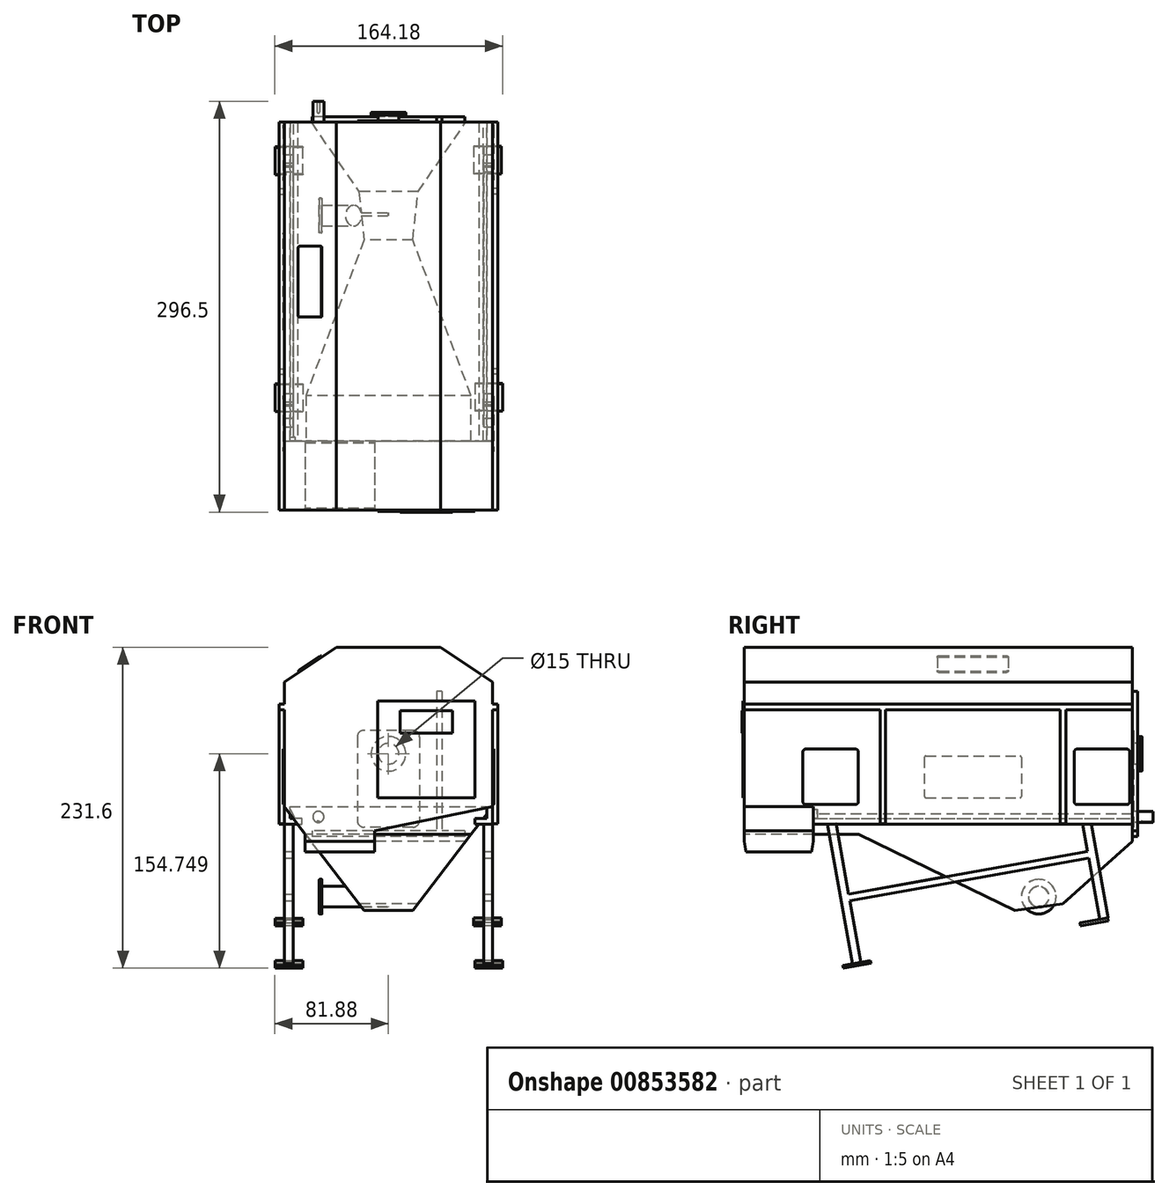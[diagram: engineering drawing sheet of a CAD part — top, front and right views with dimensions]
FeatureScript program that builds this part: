
annotation { "Feature Type Name" : "Feature", "Feature Type Description" : "" }
export const myFeature = defineFeature(function(context is Context, id is Id, definition is map)
    precondition{}
    {
        {
            var Q0;
            Q0=qCreatedBy(makeId("Front.planeOp"),FACE);
            var sketch = newSketch(context, id + "F0", { "sketchPlane" : qUnion([Q0])});
            skLineSegment(sketch, "E0", {"start": v(0, 115) * mm, "end": v(0, -89.09) * mm, "construction": true});
            skLineSegment(sketch, "E1", {"start": v(-37.5, 115) * mm, "end": v(37.5, 115) * mm});
            skLineSegment(sketch, "E2", {"start": v(37.5, 115) * mm, "end": v(75, 90) * mm});
            skLineSegment(sketch, "E3", {"start": v(75, 90) * mm, "end": v(75, 0) * mm});
            skLineSegment(sketch, "E4", {"start": v(75, 0) * mm, "end": v(-75, 0) * mm});
            skLineSegment(sketch, "E5", {"start": v(-75, 0) * mm, "end": v(-75, 90) * mm});
            skLineSegment(sketch, "E6", {"start": v(-75, 90) * mm, "end": v(-37.5, 115) * mm});
            skSolve(sketch);
        }
        {
            var Q0;
            Q0=makeQuery(id+"F0.imprint","IMPRINT",FACE,{"disambiguationData":[TD([[makeQuery(id+"F0.imprint","IMPRINT",EDGE,{"derivedFrom":sQuery(id+"F0.wireOp",EDGE,"E1")}),-1.0]])]});
            extrude(context, id + "F1", {"entities" : qUnion([Q0]), "oppositeDirection" : true, "depth" : 280 * mm, "offsetDistance" : 25 * mm});
        }
        {
            var Q0;
            Q0=qCreatedBy(makeId("Front.planeOp"),FACE);
            var sketch = newSketch(context, id + "F2", { "sketchPlane" : qUnion([Q0])});
            skLineSegment(sketch, "E7", {"start": v(-75, 0) * mm, "end": v(-60, -20) * mm});
            skLineSegment(sketch, "E8", {"start": v(-60, -20) * mm, "end": v(-60, -32.5) * mm});
            skLineSegment(sketch, "E9", {"start": v(-60, -32.5) * mm, "end": v(-10, -32.5) * mm});
            skLineSegment(sketch, "E10", {"start": v(-75, 0) * mm, "end": v(75, 0) * mm});
            skLineSegment(sketch, "E11", {"start": v(-10, -32.5) * mm, "end": v(-10, -17.5) * mm});
            skLineSegment(sketch, "E12", {"start": v(-10, -17.5) * mm, "end": v(75, 0) * mm});
            skSolve(sketch);
        }
        {
            var Q0;
            Q0=qCreatedBy(makeId("Right.planeOp"),FACE);
            var sketch = newSketch(context, id + "F3", { "sketchPlane" : qUnion([Q0])});
            skLineSegment(sketch, "E13", {"start": v(280, 0) * mm, "end": v(52.63, 0) * mm});
            skLineSegment(sketch, "E14", {"start": v(229.78, -70) * mm, "end": v(195.13, -75) * mm});
            skLineSegment(sketch, "E15", {"start": v(195.13, -75) * mm, "end": v(82.63, -20) * mm});
            skLineSegment(sketch, "E16", {"start": v(82.63, -20) * mm, "end": v(52.63, -20) * mm});
            skLineSegment(sketch, "E17", {"start": v(52.63, 0) * mm, "end": v(52.63, -20) * mm});
            skLineSegment(sketch, "E18", {"start": v(280, 0) * mm, "end": v(280, -25) * mm});
            skLineSegment(sketch, "E19", {"start": v(280, -25) * mm, "end": v(229.78, -70) * mm});
            skSolve(sketch);
        }
        {
            var Q0;
            Q0=makeQuery(id+"F3.imprint","IMPRINT",FACE,{"disambiguationData":[TD([[makeQuery(id+"F3.imprint","IMPRINT",EDGE,{"derivedFrom":sQuery(id+"F3.wireOp",EDGE,"E13")}),1.0]])]});
            extrude(context, id + "F4", {"entities" : qUnion([Q0]), "operationType" : NewBodyOperationType.ADD, "endBound" : BoundingType.SYMMETRIC, "depth" : 150 * mm, "offsetDistance" : 25 * mm});
        }
        {
            var Q0;
            Q0=makeQuery(id+"F4.boolean.opBoolean","MERGE",FACE,{"derivedFrom":[makeQuery(id+"F1.opExtrude","CAP_FACE",FACE,{"disambiguationData":[OSD([sQuery(id+"F0.wireOp",EDGE,"E1"),sQuery(id+"F0.wireOp",EDGE,"E2"),sQuery(id+"F0.wireOp",EDGE,"E3"),sQuery(id+"F0.wireOp",EDGE,"E4"),sQuery(id+"F0.wireOp",EDGE,"E5"),sQuery(id+"F0.wireOp",EDGE,"E6")])],"isStart":false}),makeQuery(id+"F4.opExtrude","SWEPT_FACE",FACE,{"disambiguationData":[OSD([sQuery(id+"F3.wireOp",EDGE,"E18")])]})]});
            var sketch = newSketch(context, id + "F5", { "sketchPlane" : qUnion([Q0])});
            skLineSegment(sketch, "E20", {"start": v(75, -75) * mm, "end": v(75, 0) * mm});
            skLineSegment(sketch, "E21", {"start": v(75, 0) * mm, "end": v(17.5, -75) * mm});
            skLineSegment(sketch, "E22", {"start": v(17.5, -75) * mm, "end": v(75, -75) * mm});
            skLineSegment(sketch, "E23", {"start": v(-75, 0) * mm, "end": v(-75, -75) * mm});
            skLineSegment(sketch, "E24", {"start": v(-75, -75) * mm, "end": v(-17.5, -75) * mm});
            skLineSegment(sketch, "E25", {"start": v(-17.5, -75) * mm, "end": v(-75, 0) * mm});
            skSolve(sketch);
        }
        {
            var Q0;
            Q0 = qSketchRegion(id + "F5", true);
            extrude(context, id + "F6", {"entities" : qUnion([Q0]), "operationType" : NewBodyOperationType.REMOVE, "oppositeDirection" : true, "depth" : 280 * mm, "offsetDistance" : 25 * mm});
        }
        {
            var Q0;
            Q0=makeQuery(id+"F2.imprint","IMPRINT",FACE,{"disambiguationData":[TD([[makeQuery(id+"F2.imprint","IMPRINT",EDGE,{"derivedFrom":sQuery(id+"F2.wireOp",EDGE,"E7")}),1.0]])]});
            extrude(context, id + "F7", {"entities" : qUnion([Q0]), "operationType" : NewBodyOperationType.ADD, "oppositeDirection" : true, "depth" : 50 * mm, "offsetDistance" : 25 * mm});
        }
        {
            var Q0;
            Q0=makeQuery(id+"F4.boolean.opBoolean","MERGE",FACE,{"derivedFrom":[makeQuery(id+"F1.opExtrude","CAP_FACE",FACE,{"disambiguationData":[OSD([sQuery(id+"F0.wireOp",EDGE,"E1"),sQuery(id+"F0.wireOp",EDGE,"E2"),sQuery(id+"F0.wireOp",EDGE,"E3"),sQuery(id+"F0.wireOp",EDGE,"E4"),sQuery(id+"F0.wireOp",EDGE,"E5"),sQuery(id+"F0.wireOp",EDGE,"E6")])],"isStart":false}),makeQuery(id+"F4.opExtrude","SWEPT_FACE",FACE,{"disambiguationData":[OSD([sQuery(id+"F3.wireOp",EDGE,"E18")])]})]});
            var sketch = newSketch(context, id + "F8", { "sketchPlane" : qUnion([Q0])});
            skLineSegment(sketch, "E26", {"start": v(75, 0) * mm, "end": v(75, -12.5) * mm});
            skLineSegment(sketch, "E27", {"start": v(75, -12.5) * mm, "end": v(62.5, -12.5) * mm});
            skLineSegment(sketch, "E28", {"start": v(62.5, -12.5) * mm, "end": v(62.5, -8.5) * mm});
            skLineSegment(sketch, "E29", {"start": v(62.5, -8.5) * mm, "end": v(71, -8.5) * mm});
            skLineSegment(sketch, "E30", {"start": v(71, -8.5) * mm, "end": v(71, 0) * mm});
            skLineSegment(sketch, "E31", {"start": v(71, 0) * mm, "end": v(75, 0) * mm});
            skSolve(sketch);
        }
        {
            var Q0;
            Q0 = qSketchRegion(id + "F8", true);
            extrude(context, id + "F9", {"entities" : qUnion([Q0]), "operationType" : NewBodyOperationType.ADD, "oppositeDirection" : true, "depth" : 230 * mm, "offsetDistance" : 25 * mm});
        }
        {
            var Q0;
            Q0=makeQuery(id+"F9.boolean.opBoolean","MERGE",FACE,{"derivedFrom":[makeQuery(id+"F4.boolean.opBoolean","MERGE",FACE,{"derivedFrom":[makeQuery(id+"F1.opExtrude","CAP_FACE",FACE,{"disambiguationData":[OSD([sQuery(id+"F0.wireOp",EDGE,"E1"),sQuery(id+"F0.wireOp",EDGE,"E2"),sQuery(id+"F0.wireOp",EDGE,"E3"),sQuery(id+"F0.wireOp",EDGE,"E4"),sQuery(id+"F0.wireOp",EDGE,"E5"),sQuery(id+"F0.wireOp",EDGE,"E6")])],"isStart":false}),makeQuery(id+"F4.opExtrude","SWEPT_FACE",FACE,{"disambiguationData":[OSD([sQuery(id+"F3.wireOp",EDGE,"E18")])]})]}),makeQuery(id+"F9.opExtrude","CAP_FACE",FACE,{"disambiguationData":[OSD([sQuery(id+"F8.wireOp",EDGE,"E26"),sQuery(id+"F8.wireOp",EDGE,"E27"),sQuery(id+"F8.wireOp",EDGE,"E28"),sQuery(id+"F8.wireOp",EDGE,"E29"),sQuery(id+"F8.wireOp",EDGE,"E30"),sQuery(id+"F8.wireOp",EDGE,"E31")])],"isStart":true})]});
            var sketch = newSketch(context, id + "F10", { "sketchPlane" : qUnion([Q0])});
            skLineSegment(sketch, "E32", {"start": v(-75, 0) * mm, "end": v(-75, -12.5) * mm});
            skLineSegment(sketch, "E33", {"start": v(-75, -12.5) * mm, "end": v(-62.5, -12.5) * mm});
            skLineSegment(sketch, "E34", {"start": v(-62.5, -12.5) * mm, "end": v(-62.5, -8.5) * mm});
            skLineSegment(sketch, "E35", {"start": v(-62.5, -8.5) * mm, "end": v(-71, -8.5) * mm});
            skLineSegment(sketch, "E36", {"start": v(-71, -8.5) * mm, "end": v(-71, 0) * mm});
            skLineSegment(sketch, "E37", {"start": v(-71, 0) * mm, "end": v(-75, 0) * mm});
            skSolve(sketch);
        }
        {
            var Q0;
            Q0 = qSketchRegion(id + "F10", true);
            extrude(context, id + "F11", {"entities" : qUnion([Q0]), "operationType" : NewBodyOperationType.ADD, "oppositeDirection" : true, "depth" : 230 * mm, "offsetDistance" : 25 * mm});
        }
        {
            var Q0;
            Q0=makeQuery(id+"F4.boolean.opBoolean","MERGE",FACE,{"derivedFrom":[makeQuery(id+"F1.opExtrude","SWEPT_FACE",FACE,{"disambiguationData":[OSD([sQuery(id+"F0.wireOp",EDGE,"E3")])]}),makeQuery(id+"F4.opExtrude","CAP_FACE",FACE,{"disambiguationData":[OSD([sQuery(id+"F3.wireOp",EDGE,"E13"),sQuery(id+"F3.wireOp",EDGE,"E14"),sQuery(id+"F3.wireOp",EDGE,"E15"),sQuery(id+"F3.wireOp",EDGE,"E16"),sQuery(id+"F3.wireOp",EDGE,"E17"),sQuery(id+"F3.wireOp",EDGE,"E18"),sQuery(id+"F3.wireOp",EDGE,"E19")])],"isStart":false})]});
            var sketch = newSketch(context, id + "F12", { "sketchPlane" : qUnion([Q0])});
            skLineSegment(sketch, "E38", {"start": v(60, -12.5) * mm, "end": v(78.1, -113.4) * mm});
            skLineSegment(sketch, "E39", {"start": v(78.1, -113.4) * mm, "end": v(84.24, -112.29) * mm});
            skLineSegment(sketch, "E40", {"start": v(84.24, -112.29) * mm, "end": v(76.3, -68) * mm});
            skLineSegment(sketch, "E41", {"start": v(76.3, -68) * mm, "end": v(248.55, -37.1) * mm});
            skLineSegment(sketch, "E42", {"start": v(248.55, -37.1) * mm, "end": v(256.5, -81.4) * mm});
            skLineSegment(sketch, "E43", {"start": v(256.5, -81.4) * mm, "end": v(262.65, -80.3) * mm});
            skLineSegment(sketch, "E44", {"start": v(262.65, -80.3) * mm, "end": v(250.56, -12.87) * mm});
            skLineSegment(sketch, "E45", {"start": v(247.67, -32.19) * mm, "end": v(75.42, -63.07) * mm});
            skLineSegment(sketch, "E46", {"start": v(75.42, -63.07) * mm, "end": v(66.33, -12.38) * mm});
            skLineSegment(sketch, "E47", {"start": v(66.33, -12.38) * mm, "end": v(60, -12.5) * mm});
            skLineSegment(sketch, "E48", {"start": v(247.67, -32.19) * mm, "end": v(244.14, -12.5) * mm});
            skLineSegment(sketch, "E49", {"start": v(244.14, -12.5) * mm, "end": v(250.56, -12.87) * mm});
            skLineSegment(sketch, "E50", {"start": v(50, -12.5) * mm, "end": v(60, -12.5) * mm, "construction": true});
            skSolve(sketch);
        }
        {
            var Q0;
            Q0 = qSketchRegion(id + "F12", true);
            extrude(context, id + "F13", {"entities" : qUnion([Q0]), "oppositeDirection" : true, "depth" : 6.25 * mm, "offsetDistance" : 25 * mm});
        }
        {
            var Q0;
            Q0=makeQuery(id+"F13.opExtrude","SWEPT_BODY",BODY,{"disambiguationData":[OSD([sQuery(id+"F12.wireOp",EDGE,"E38"),sQuery(id+"F12.wireOp",EDGE,"E39"),sQuery(id+"F12.wireOp",EDGE,"E40"),sQuery(id+"F12.wireOp",EDGE,"E41"),sQuery(id+"F12.wireOp",EDGE,"E42"),sQuery(id+"F12.wireOp",EDGE,"E43"),sQuery(id+"F12.wireOp",EDGE,"E44"),sQuery(id+"F12.wireOp",EDGE,"E45"),sQuery(id+"F12.wireOp",EDGE,"E46"),sQuery(id+"F12.wireOp",EDGE,"E47"),sQuery(id+"F12.wireOp",EDGE,"E48"),sQuery(id+"F12.wireOp",EDGE,"E49")])]});
            transform(context, id + "F14", {"entities" : qUnion([Q0]), "transformType" : TransformType.TRANSLATION_3D, "dx" : 150 * mm, "dy" : 0 * mm, "dz" : 0 * mm, "makeCopy" : true});
        }
        {
            var Q0;
            Q0=makeQuery(id+"F14.opPattern","COPY",BODY,{"derivedFrom":makeQuery(id+"F13.opExtrude","SWEPT_BODY",BODY,{"disambiguationData":[OSD([sQuery(id+"F12.wireOp",EDGE,"E38"),sQuery(id+"F12.wireOp",EDGE,"E39"),sQuery(id+"F12.wireOp",EDGE,"E40"),sQuery(id+"F12.wireOp",EDGE,"E41"),sQuery(id+"F12.wireOp",EDGE,"E42"),sQuery(id+"F12.wireOp",EDGE,"E43"),sQuery(id+"F12.wireOp",EDGE,"E44"),sQuery(id+"F12.wireOp",EDGE,"E45"),sQuery(id+"F12.wireOp",EDGE,"E46"),sQuery(id+"F12.wireOp",EDGE,"E47"),sQuery(id+"F12.wireOp",EDGE,"E48"),sQuery(id+"F12.wireOp",EDGE,"E49")])]}),"instanceName":"1"});
            deleteBodies(context, id + "F15", {"entities" : qUnion([Q0])});
        }
        {
            var Q0;
            Q0=makeQuery(id+"F13.opExtrude","SWEPT_BODY",BODY,{"disambiguationData":[OSD([sQuery(id+"F12.wireOp",EDGE,"E38"),sQuery(id+"F12.wireOp",EDGE,"E39"),sQuery(id+"F12.wireOp",EDGE,"E40"),sQuery(id+"F12.wireOp",EDGE,"E41"),sQuery(id+"F12.wireOp",EDGE,"E42"),sQuery(id+"F12.wireOp",EDGE,"E43"),sQuery(id+"F12.wireOp",EDGE,"E44"),sQuery(id+"F12.wireOp",EDGE,"E45"),sQuery(id+"F12.wireOp",EDGE,"E46"),sQuery(id+"F12.wireOp",EDGE,"E47"),sQuery(id+"F12.wireOp",EDGE,"E48"),sQuery(id+"F12.wireOp",EDGE,"E49")])]});
            transform(context, id + "F16", {"entities" : qUnion([Q0]), "transformType" : TransformType.TRANSLATION_3D, "dx" : -143.75 * mm, "dy" : 0 * mm, "dz" : 0 * mm, "makeCopy" : true});
        }
        {
            var Q0;
            Q0=makeQuery(id+"F7.opExtrude","SWEPT_FACE",FACE,{"disambiguationData":[OSD([sQuery(id+"F2.wireOp",EDGE,"E11")])]});
            var sketch = newSketch(context, id + "F17", { "sketchPlane" : qUnion([Q0])});
            skLineSegment(sketch, "E51.bottom", {"start": v(-2.7, -21.26) * mm, "end": v(-0.73, -20.9) * mm});
            skLineSegment(sketch, "E51.top", {"start": v(-0.05, -36.03) * mm, "end": v(1.91, -35.67) * mm});
            skLineSegment(sketch, "E51.left", {"start": v(-2.7, -21.26) * mm, "end": v(-0.05, -36.03) * mm});
            skLineSegment(sketch, "E51.right", {"start": v(-0.73, -20.9) * mm, "end": v(1.91, -35.67) * mm});
            skSolve(sketch);
        }
        {
            var Q0;
            Q0 = qSketchRegion(id + "F17", true);
            extrude(context, id + "F18", {"entities" : qUnion([Q0]), "operationType" : NewBodyOperationType.REMOVE, "oppositeDirection" : true, "depth" : 50 * mm, "offsetDistance" : 25 * mm});
        }
        {
            var Q0;
            Q0=makeQuery(id+"F7.opExtrude","SWEPT_FACE",FACE,{"disambiguationData":[OSD([sQuery(id+"F2.wireOp",EDGE,"E8")])]});
            var sketch = newSketch(context, id + "F19", { "sketchPlane" : qUnion([Q0])});
            skLineSegment(sketch, "E52.bottom", {"start": v(-52.12, -24.53) * mm, "end": v(-50.15, -24.17) * mm});
            skLineSegment(sketch, "E52.top", {"start": v(-49.47, -39.3) * mm, "end": v(-47.5, -38.94) * mm});
            skLineSegment(sketch, "E52.left", {"start": v(-52.12, -24.53) * mm, "end": v(-49.47, -39.3) * mm});
            skLineSegment(sketch, "E52.right", {"start": v(-50.15, -24.17) * mm, "end": v(-47.5, -38.94) * mm});
            skLineSegment(sketch, "E53", {"start": v(0, -25) * mm, "end": v(-50, -25) * mm, "construction": true});
            skSolve(sketch);
        }
        {
            var Q0;
            Q0 = qSketchRegion(id + "F19", true);
            extrude(context, id + "F20", {"entities" : qUnion([Q0]), "operationType" : NewBodyOperationType.REMOVE, "oppositeDirection" : true, "depth" : 50 * mm, "offsetDistance" : 25 * mm});
        }
        {
            var Q0;
            Q0=qCreatedBy(makeId("Right.planeOp"),FACE);
            var sketch = newSketch(context, id + "F21", { "sketchPlane" : qUnion([Q0])});
            skCircle(sketch, "E54", {"center": v(212.51, -65) * mm, "radius": 7.5 * mm});
            skPoint(sketch, "E54.first.point", {"position": v(212.45, -72.5) * mm});
            skPoint(sketch, "E54.second.point", {"position": v(213.2, -57.53) * mm});
            skPoint(sketch, "E54.third.point", {"position": v(205.16, -63.52) * mm});
            skSolve(sketch);
        }
        {
            var Q0;
            Q0 = qSketchRegion(id + "F21", true);
            extrude(context, id + "F22", {"entities" : qUnion([Q0]), "operationType" : NewBodyOperationType.ADD, "oppositeDirection" : true, "depth" : 50 * mm, "offsetDistance" : 25 * mm});
        }
        {
            var Q0;
            Q0=makeQuery(id+"F22.opExtrude","CAP_FACE",FACE,{"disambiguationData":[OSD([sQuery(id+"F21.wireOp",EDGE,"E54")])],"isStart":false});
            var sketch = newSketch(context, id + "F23", { "sketchPlane" : qUnion([Q0])});
            skCircle(sketch, "E55", {"center": v(-212.51, -65) * mm, "radius": 12.5 * mm});
            skSolve(sketch);
        }
        {
            var Q0;
            Q0 = qSketchRegion(id + "F23", true);
            extrude(context, id + "F24", {"entities" : qUnion([Q0]), "operationType" : NewBodyOperationType.ADD, "oppositeDirection" : true, "depth" : 2 * mm, "offsetDistance" : 25 * mm});
        }
        {
            var Q0;
            Q0=makeQuery(id+"F24.opExtrude","SWEPT_FACE",FACE,{"disambiguationData":[OSD([sQuery(id+"F23.wireOp",EDGE,"E55")])]});
            fillet(context, id + "F25", {"entities" : qUnion([Q0]), "radius" : 0.25 * mm, "tangentPropagation" : true, "allowEdgeOverflow" : false});
        }
        {
            var Q0;
            Q0=makeQuery(id+"F11.boolean.opBoolean","MERGE",FACE,{"derivedFrom":[makeQuery(id+"F9.boolean.opBoolean","MERGE",FACE,{"derivedFrom":[makeQuery(id+"F4.boolean.opBoolean","MERGE",FACE,{"derivedFrom":[makeQuery(id+"F1.opExtrude","CAP_FACE",FACE,{"disambiguationData":[OSD([sQuery(id+"F0.wireOp",EDGE,"E1"),sQuery(id+"F0.wireOp",EDGE,"E2"),sQuery(id+"F0.wireOp",EDGE,"E3"),sQuery(id+"F0.wireOp",EDGE,"E4"),sQuery(id+"F0.wireOp",EDGE,"E5"),sQuery(id+"F0.wireOp",EDGE,"E6")])],"isStart":false}),makeQuery(id+"F4.opExtrude","SWEPT_FACE",FACE,{"disambiguationData":[OSD([sQuery(id+"F3.wireOp",EDGE,"E18")])]})]}),makeQuery(id+"F9.opExtrude","CAP_FACE",FACE,{"disambiguationData":[OSD([sQuery(id+"F8.wireOp",EDGE,"E26"),sQuery(id+"F8.wireOp",EDGE,"E27"),sQuery(id+"F8.wireOp",EDGE,"E28"),sQuery(id+"F8.wireOp",EDGE,"E29"),sQuery(id+"F8.wireOp",EDGE,"E30"),sQuery(id+"F8.wireOp",EDGE,"E31")])],"isStart":true})]}),makeQuery(id+"F11.opExtrude","CAP_FACE",FACE,{"disambiguationData":[OSD([sQuery(id+"F10.wireOp",EDGE,"E32"),sQuery(id+"F10.wireOp",EDGE,"E33"),sQuery(id+"F10.wireOp",EDGE,"E34"),sQuery(id+"F10.wireOp",EDGE,"E35"),sQuery(id+"F10.wireOp",EDGE,"E36"),sQuery(id+"F10.wireOp",EDGE,"E37")])],"isStart":true})]});
            var sketch = newSketch(context, id + "F26", { "sketchPlane" : qUnion([Q0])});
            skLineSegment(sketch, "E56.bottom", {"start": v(-17.5, 55.1) * mm, "end": v(17.5, 55.1) * mm});
            skLineSegment(sketch, "E56.top", {"start": v(-17.5, -14.9) * mm, "end": v(17.5, -14.9) * mm});
            skLineSegment(sketch, "E56.left", {"start": v(-22.5, 50.1) * mm, "end": v(-22.5, -9.9) * mm});
            skLineSegment(sketch, "E56.right", {"start": v(22.5, 50.1) * mm, "end": v(22.5, -9.9) * mm});
            skPoint(sketch, "E57.visualSharp", {"position": v(22.5, 55.1) * mm});
            skArc(sketch, "E57.filletArc", {"start": v(22.5, 50.1) * mm, "mid": v(21.04, 53.64) * mm, "end": v(17.5, 55.1) * mm});
            skPoint(sketch, "E58.visualSharp", {"position": v(-22.5, 55.1) * mm});
            skArc(sketch, "E58.filletArc", {"start": v(-17.5, 55.1) * mm, "mid": v(-21.04, 53.64) * mm, "end": v(-22.5, 50.1) * mm});
            skPoint(sketch, "E59.visualSharp", {"position": v(-22.5, -14.9) * mm});
            skArc(sketch, "E59.filletArc", {"start": v(-22.5, -9.9) * mm, "mid": v(-21.04, -13.43) * mm, "end": v(-17.5, -14.9) * mm});
            skPoint(sketch, "E60.visualSharp", {"position": v(22.5, -14.9) * mm});
            skArc(sketch, "E60.filletArc", {"start": v(17.5, -14.9) * mm, "mid": v(21.04, -13.43) * mm, "end": v(22.5, -9.9) * mm});
            skLineSegment(sketch, "E61", {"start": v(0, -25) * mm, "end": v(0, 111.63) * mm, "construction": true});
            skCircle(sketch, "E62", {"center": v(0, 38.15) * mm, "radius": 7.5 * mm});
            skSolve(sketch);
        }
        {
            var Q0;
            Q0=makeQuery(id+"F26.imprint","IMPRINT",FACE,{"disambiguationData":[TD([[makeQuery(id+"F26.imprint","IMPRINT",EDGE,{"derivedFrom":sQuery(id+"F26.wireOp",EDGE,"E62")}),1.0]])]});
            var Q1;
            Q1=sQuery(id+"F26.wireOp",EDGE,"E62");
            extrude(context, id + "F27", {"entities" : qUnion([Q0]), "surfaceEntities" : qUnion([Q1]), "depth" : 5 * mm, "offsetDistance" : 25 * mm});
        }
        {
            var Q0;
            Q0=makeQuery(id+"F26.imprint","IMPRINT",FACE,{"disambiguationData":[TD([[makeQuery(id+"F26.imprint","IMPRINT",EDGE,{"derivedFrom":sQuery(id+"F26.wireOp",EDGE,"E56.bottom")}),-1.0]])]});
            extrude(context, id + "F28", {"entities" : qUnion([Q0]), "depth" : 1 * mm, "offsetDistance" : 25 * mm});
        }
        {
            var Q0;
            Q0=makeQuery(id+"F27.opExtrude","CAP_FACE",FACE,{"disambiguationData":[OSD([sQuery(id+"F26.wireOp",EDGE,"E62")])],"isStart":false});
            var sketch = newSketch(context, id + "F29", { "sketchPlane" : qUnion([Q0])});
            skCircle(sketch, "E63", {"center": v(0, 38.15) * mm, "radius": 12.5 * mm});
            skSolve(sketch);
        }
        {
            var Q0;
            Q0 = qSketchRegion(id + "F29", true);
            extrude(context, id + "F30", {"entities" : qUnion([Q0]), "operationType" : NewBodyOperationType.ADD, "depth" : 2 * mm, "offsetDistance" : 25 * mm});
        }
        {
            var Q0;
            Q0=makeQuery(id+"F30.opExtrude","SWEPT_FACE",FACE,{"disambiguationData":[OSD([sQuery(id+"F29.wireOp",EDGE,"E63")])]});
            fillet(context, id + "F31", {"entities" : qUnion([Q0]), "radius" : 0.25 * mm, "tangentPropagation" : true, "allowEdgeOverflow" : false});
        }
        {
            var Q0;
            Q0=makeQuery(id+"F11.boolean.opBoolean","MERGE",FACE,{"derivedFrom":[makeQuery(id+"F9.boolean.opBoolean","MERGE",FACE,{"derivedFrom":[makeQuery(id+"F4.boolean.opBoolean","MERGE",FACE,{"derivedFrom":[makeQuery(id+"F1.opExtrude","CAP_FACE",FACE,{"disambiguationData":[OSD([sQuery(id+"F0.wireOp",EDGE,"E1"),sQuery(id+"F0.wireOp",EDGE,"E2"),sQuery(id+"F0.wireOp",EDGE,"E3"),sQuery(id+"F0.wireOp",EDGE,"E4"),sQuery(id+"F0.wireOp",EDGE,"E5"),sQuery(id+"F0.wireOp",EDGE,"E6")])],"isStart":false}),makeQuery(id+"F4.opExtrude","SWEPT_FACE",FACE,{"disambiguationData":[OSD([sQuery(id+"F3.wireOp",EDGE,"E18")])]})]}),makeQuery(id+"F9.opExtrude","CAP_FACE",FACE,{"disambiguationData":[OSD([sQuery(id+"F8.wireOp",EDGE,"E26"),sQuery(id+"F8.wireOp",EDGE,"E27"),sQuery(id+"F8.wireOp",EDGE,"E28"),sQuery(id+"F8.wireOp",EDGE,"E29"),sQuery(id+"F8.wireOp",EDGE,"E30"),sQuery(id+"F8.wireOp",EDGE,"E31")])],"isStart":true})]}),makeQuery(id+"F11.opExtrude","CAP_FACE",FACE,{"disambiguationData":[OSD([sQuery(id+"F10.wireOp",EDGE,"E32"),sQuery(id+"F10.wireOp",EDGE,"E33"),sQuery(id+"F10.wireOp",EDGE,"E34"),sQuery(id+"F10.wireOp",EDGE,"E35"),sQuery(id+"F10.wireOp",EDGE,"E36"),sQuery(id+"F10.wireOp",EDGE,"E37")])],"isStart":true})]});
            var sketch = newSketch(context, id + "F32", { "sketchPlane" : qUnion([Q0])});
            skLineSegment(sketch, "E64", {"start": v(-55, -25) * mm, "end": v(-55, -14.86) * mm, "construction": true});
            skLineSegment(sketch, "E65", {"start": v(-55, -14.86) * mm, "end": v(-55, -19.93) * mm, "construction": true});
            skLineSegment(sketch, "E66.bottom", {"start": v(-55, -17.4) * mm, "end": v(55, -17.4) * mm});
            skLineSegment(sketch, "E66.top", {"start": v(-55, -21.4) * mm, "end": v(55, -21.4) * mm});
            skLineSegment(sketch, "E66.left", {"start": v(-55, -17.4) * mm, "end": v(-55, -21.4) * mm});
            skLineSegment(sketch, "E66.right", {"start": v(55, -17.4) * mm, "end": v(55, -21.4) * mm});
            skLineSegment(sketch, "E67", {"start": v(0, -25) * mm, "end": v(0, -21.4) * mm, "construction": true});
            skLineSegment(sketch, "E68", {"start": v(-36.67, -17.4) * mm, "end": v(-36.67, 83.32) * mm, "construction": true});
            skLineSegment(sketch, "E69.bottom", {"start": v(-38.67, 83.32) * mm, "end": v(-34.67, 83.32) * mm});
            skLineSegment(sketch, "E69.top", {"start": v(-38.67, -17.4) * mm, "end": v(-34.67, -17.4) * mm});
            skLineSegment(sketch, "E69.left", {"start": v(-38.67, 83.32) * mm, "end": v(-38.67, -17.4) * mm});
            skLineSegment(sketch, "E69.right", {"start": v(-34.67, 83.32) * mm, "end": v(-34.67, -17.4) * mm});
            skPoint(sketch, "E69.middle", {"position": v(-36.67, 32.96) * mm});
            skSolve(sketch);
        }
        {
            var Q0;
            Q0=makeQuery(id+"F32.imprint","IMPRINT",FACE,{"disambiguationData":[TD([[makeQuery(id+"F32.imprint","IMPRINT",EDGE,{"derivedFrom":sQuery(id+"F32.wireOp",EDGE,"E66.top")}),1.0]])]});
            var Q1;
            Q1=makeQuery(id+"F32.imprint","IMPRINT",FACE,{"disambiguationData":[TD([[makeQuery(id+"F32.imprint","IMPRINT",EDGE,{"derivedFrom":sQuery(id+"F32.wireOp",EDGE,"E69.bottom")}),-1.0]])]});
            extrude(context, id + "F33", {"entities" : qUnion([Q0, Q1]), "operationType" : NewBodyOperationType.ADD, "depth" : 4 * mm, "offsetDistance" : 25 * mm});
        }
        {
            var Q0;
            Q0=makeQuery(id+"F11.boolean.opBoolean","MERGE",FACE,{"derivedFrom":[makeQuery(id+"F4.boolean.opBoolean","MERGE",FACE,{"derivedFrom":[makeQuery(id+"F1.opExtrude","SWEPT_FACE",FACE,{"disambiguationData":[OSD([sQuery(id+"F0.wireOp",EDGE,"E3")])]}),makeQuery(id+"F4.opExtrude","CAP_FACE",FACE,{"disambiguationData":[OSD([sQuery(id+"F3.wireOp",EDGE,"E13"),sQuery(id+"F3.wireOp",EDGE,"E14"),sQuery(id+"F3.wireOp",EDGE,"E15"),sQuery(id+"F3.wireOp",EDGE,"E16"),sQuery(id+"F3.wireOp",EDGE,"E17"),sQuery(id+"F3.wireOp",EDGE,"E18"),sQuery(id+"F3.wireOp",EDGE,"E19")])],"isStart":false})]}),makeQuery(id+"F11.opExtrude","SWEPT_FACE",FACE,{"disambiguationData":[OSD([sQuery(id+"F10.wireOp",EDGE,"E32")])]})]});
            var sketch = newSketch(context, id + "F34", { "sketchPlane" : qUnion([Q0])});
            skLineSegment(sketch, "E70.bottom", {"start": v(280, 70) * mm, "end": v(0, 70) * mm});
            skLineSegment(sketch, "E70.top", {"start": v(280, 74) * mm, "end": v(0, 74) * mm});
            skLineSegment(sketch, "E70.left", {"start": v(280, 70) * mm, "end": v(280, 74) * mm});
            skLineSegment(sketch, "E70.right", {"start": v(0, 70) * mm, "end": v(0, 74) * mm});
            skSolve(sketch);
        }
        {
            var Q0;
            Q0=makeQuery(id+"F34.imprint","IMPRINT",FACE,{"disambiguationData":[TD([[makeQuery(id+"F34.imprint","IMPRINT",EDGE,{"derivedFrom":sQuery(id+"F34.wireOp",EDGE,"E70.bottom")}),-1.0]])]});
            extrude(context, id + "F35", {"entities" : qUnion([Q0]), "operationType" : NewBodyOperationType.ADD, "depth" : 4 * mm, "offsetDistance" : 25 * mm});
        }
        {
            var Q0;
            Q0=makeQuery(id+"F9.boolean.opBoolean","MERGE",FACE,{"derivedFrom":[makeQuery(id+"F4.boolean.opBoolean","MERGE",FACE,{"derivedFrom":[makeQuery(id+"F1.opExtrude","SWEPT_FACE",FACE,{"disambiguationData":[OSD([sQuery(id+"F0.wireOp",EDGE,"E5")])]}),makeQuery(id+"F4.opExtrude","CAP_FACE",FACE,{"disambiguationData":[OSD([sQuery(id+"F3.wireOp",EDGE,"E13"),sQuery(id+"F3.wireOp",EDGE,"E14"),sQuery(id+"F3.wireOp",EDGE,"E15"),sQuery(id+"F3.wireOp",EDGE,"E16"),sQuery(id+"F3.wireOp",EDGE,"E17"),sQuery(id+"F3.wireOp",EDGE,"E18"),sQuery(id+"F3.wireOp",EDGE,"E19")])],"isStart":true})]}),makeQuery(id+"F9.opExtrude","SWEPT_FACE",FACE,{"disambiguationData":[OSD([sQuery(id+"F8.wireOp",EDGE,"E26")])]})]});
            var sketch = newSketch(context, id + "F36", { "sketchPlane" : qUnion([Q0])});
            skLineSegment(sketch, "E71.bottom", {"start": v(-280, 74) * mm, "end": v(0, 74) * mm});
            skLineSegment(sketch, "E71.top", {"start": v(-280, 70) * mm, "end": v(0, 70) * mm});
            skLineSegment(sketch, "E71.left", {"start": v(-280, 70) * mm, "end": v(-280, 74) * mm});
            skLineSegment(sketch, "E71.right", {"start": v(0, 70) * mm, "end": v(0, 74) * mm});
            skSolve(sketch);
        }
        {
            var Q0;
            Q0=makeQuery(id+"F36.imprint","IMPRINT",FACE,{"disambiguationData":[TD([[makeQuery(id+"F36.imprint","IMPRINT",EDGE,{"derivedFrom":sQuery(id+"F36.wireOp",EDGE,"E71.bottom")}),-1.0]])]});
            extrude(context, id + "F37", {"entities" : qUnion([Q0]), "operationType" : NewBodyOperationType.ADD, "depth" : 4 * mm, "offsetDistance" : 25 * mm});
        }
        {
            var Q0;
            {var subQ5=sQuery(id+"F8.wireOp",EDGE,"E26");var subQ7=sQuery(id+"F0.wireOp",EDGE,"E5");var subQ12=sQuery(id+"F2.wireOp",EDGE,"E7");var subQ13=sQuery(id+"F3.wireOp",EDGE,"E18");Q0=makeQuery(id+"F37.boolean.opBoolean","SPLIT",FACE,{"disambiguationData":[TD([makeQuery(id+"F7.opExtrude","SWEPT_FACE",FACE,{"disambiguationData":[OSD([subQ12])]})])],"derivedFrom":makeQuery(id+"F9.boolean.opBoolean","MERGE",FACE,{"derivedFrom":[makeQuery(id+"F4.boolean.opBoolean","MERGE",FACE,{"derivedFrom":[makeQuery(id+"F1.opExtrude","SWEPT_FACE",FACE,{"disambiguationData":[OSD([subQ7])]}),makeQuery(id+"F4.opExtrude","CAP_FACE",FACE,{"disambiguationData":[OSD([sQuery(id+"F3.wireOp",EDGE,"E13"),sQuery(id+"F3.wireOp",EDGE,"E14"),sQuery(id+"F3.wireOp",EDGE,"E15"),sQuery(id+"F3.wireOp",EDGE,"E16"),sQuery(id+"F3.wireOp",EDGE,"E17"),subQ13,sQuery(id+"F3.wireOp",EDGE,"E19")])],"isStart":true})]}),makeQuery(id+"F9.opExtrude","SWEPT_FACE",FACE,{"disambiguationData":[OSD([subQ5])]})]})});}
            var sketch = newSketch(context, id + "F38", { "sketchPlane" : qUnion([Q0])});
            skLineSegment(sketch, "E72", {"start": v(-230, -12.5) * mm, "end": v(-230, 89.6) * mm, "construction": true});
            skLineSegment(sketch, "E73", {"start": v(-100, -12.5) * mm, "end": v(-100, 89.95) * mm, "construction": true});
            skLineSegment(sketch, "E74", {"start": v(-230, 38.55) * mm, "end": v(-100, 38.72) * mm, "construction": true});
            skLineSegment(sketch, "E75.bottom", {"start": v(-232, 89.72) * mm, "end": v(-228, 89.72) * mm});
            skLineSegment(sketch, "E75.top", {"start": v(-232, -12.62) * mm, "end": v(-228, -12.62) * mm});
            skLineSegment(sketch, "E75.left", {"start": v(-232, 89.72) * mm, "end": v(-232, -12.62) * mm});
            skLineSegment(sketch, "E75.right", {"start": v(-228, 89.72) * mm, "end": v(-228, -12.62) * mm});
            skPoint(sketch, "E75.middle", {"position": v(-230, 38.55) * mm});
            skLineSegment(sketch, "E76.bottom", {"start": v(-102, 89.72) * mm, "end": v(-98, 89.72) * mm});
            skLineSegment(sketch, "E76.top", {"start": v(-102, -12.28) * mm, "end": v(-98, -12.28) * mm});
            skLineSegment(sketch, "E76.left", {"start": v(-102, 89.72) * mm, "end": v(-102, -12.28) * mm});
            skLineSegment(sketch, "E76.right", {"start": v(-98, 89.72) * mm, "end": v(-98, -12.28) * mm});
            skPoint(sketch, "E76.middle", {"position": v(-100, 38.72) * mm});
            skLineSegment(sketch, "E77", {"start": v(-280, 21.5) * mm, "end": v(0, 21.5) * mm, "construction": true});
            skLineSegment(sketch, "E78", {"start": v(-280, 21.5) * mm, "end": v(-258, 21.5) * mm, "construction": true});
            skLineSegment(sketch, "E79.bottom", {"start": v(-275.5, 41.5) * mm, "end": v(-240.5, 41.5) * mm});
            skLineSegment(sketch, "E79.top", {"start": v(-275.5, 1.5) * mm, "end": v(-240.5, 1.5) * mm});
            skLineSegment(sketch, "E79.left", {"start": v(-278, 39) * mm, "end": v(-278, 4) * mm});
            skLineSegment(sketch, "E79.right", {"start": v(-238, 39) * mm, "end": v(-238, 4) * mm});
            skPoint(sketch, "E79.middle", {"position": v(-258, 21.5) * mm});
            skPoint(sketch, "E80.visualSharp", {"position": v(-278, 41.5) * mm});
            skArc(sketch, "E80.filletArc", {"start": v(-275.5, 41.5) * mm, "mid": v(-277.27, 40.77) * mm, "end": v(-278, 39) * mm});
            skPoint(sketch, "E81.visualSharp", {"position": v(-238, 41.5) * mm});
            skArc(sketch, "E81.filletArc", {"start": v(-238, 39) * mm, "mid": v(-238.73, 40.77) * mm, "end": v(-240.5, 41.5) * mm});
            skPoint(sketch, "E82.visualSharp", {"position": v(-238, 1.5) * mm});
            skArc(sketch, "E82.filletArc", {"start": v(-240.5, 1.5) * mm, "mid": v(-238.73, 2.23) * mm, "end": v(-238, 4) * mm});
            skPoint(sketch, "E83.visualSharp", {"position": v(-278, 1.5) * mm});
            skArc(sketch, "E83.filletArc", {"start": v(-278, 4) * mm, "mid": v(-277.27, 2.23) * mm, "end": v(-275.5, 1.5) * mm});
            skLineSegment(sketch, "E84", {"start": v(0, 21.5) * mm, "end": v(-62.5, 21.5) * mm, "construction": true});
            skLineSegment(sketch, "E85.bottom", {"start": v(-80, 41.5) * mm, "end": v(-45, 41.5) * mm});
            skLineSegment(sketch, "E85.top", {"start": v(-80, 1.5) * mm, "end": v(-45, 1.5) * mm});
            skLineSegment(sketch, "E85.left", {"start": v(-82.5, 39) * mm, "end": v(-82.5, 4) * mm});
            skLineSegment(sketch, "E85.right", {"start": v(-42.5, 39) * mm, "end": v(-42.5, 4) * mm});
            skPoint(sketch, "E85.middle", {"position": v(-62.5, 21.5) * mm});
            skPoint(sketch, "E86.visualSharp", {"position": v(-82.5, 41.5) * mm});
            skArc(sketch, "E86.filletArc", {"start": v(-80, 41.5) * mm, "mid": v(-81.77, 40.77) * mm, "end": v(-82.5, 39) * mm});
            skPoint(sketch, "E87.visualSharp", {"position": v(-42.5, 41.5) * mm});
            skArc(sketch, "E87.filletArc", {"start": v(-42.5, 39) * mm, "mid": v(-43.23, 40.77) * mm, "end": v(-45, 41.5) * mm});
            skPoint(sketch, "E88.visualSharp", {"position": v(-42.5, 1.5) * mm});
            skArc(sketch, "E88.filletArc", {"start": v(-45, 1.5) * mm, "mid": v(-43.23, 2.23) * mm, "end": v(-42.5, 4) * mm});
            skPoint(sketch, "E89.visualSharp", {"position": v(-82.5, 1.5) * mm});
            skArc(sketch, "E89.filletArc", {"start": v(-82.5, 4) * mm, "mid": v(-81.77, 2.23) * mm, "end": v(-80, 1.5) * mm});
            skLineSegment(sketch, "E90", {"start": v(-165, 38.64) * mm, "end": v(-165.07, 90.55) * mm, "construction": true});
            skLineSegment(sketch, "E91", {"start": v(-165.07, 90.55) * mm, "end": v(-165, 38.64) * mm, "construction": true});
            skLineSegment(sketch, "E92", {"start": v(-165, 38.64) * mm, "end": v(-165, 21.5) * mm, "construction": true});
            skLineSegment(sketch, "E93.bottom", {"start": v(-131, 36.5) * mm, "end": v(-199, 36.5) * mm});
            skLineSegment(sketch, "E93.top", {"start": v(-131, 6.5) * mm, "end": v(-199, 6.5) * mm});
            skLineSegment(sketch, "E93.left", {"start": v(-130, 35.5) * mm, "end": v(-130, 7.5) * mm});
            skLineSegment(sketch, "E93.right", {"start": v(-200, 35.5) * mm, "end": v(-200, 7.5) * mm});
            skPoint(sketch, "E93.middle", {"position": v(-165, 21.5) * mm});
            skPoint(sketch, "E94.visualSharp", {"position": v(-200, 36.5) * mm});
            skArc(sketch, "E94.filletArc", {"start": v(-199, 36.5) * mm, "mid": v(-199.7, 36.2) * mm, "end": v(-200, 35.5) * mm});
            skPoint(sketch, "E95.visualSharp", {"position": v(-130, 36.5) * mm});
            skArc(sketch, "E95.filletArc", {"start": v(-130, 35.5) * mm, "mid": v(-130.3, 36.2) * mm, "end": v(-131, 36.5) * mm});
            skPoint(sketch, "E96.visualSharp", {"position": v(-130, 6.5) * mm});
            skArc(sketch, "E96.filletArc", {"start": v(-131, 6.5) * mm, "mid": v(-130.3, 6.8) * mm, "end": v(-130, 7.5) * mm});
            skPoint(sketch, "E97.visualSharp", {"position": v(-200, 6.5) * mm});
            skArc(sketch, "E97.filletArc", {"start": v(-200, 7.5) * mm, "mid": v(-199.7, 6.8) * mm, "end": v(-199, 6.5) * mm});
            skSolve(sketch);
        }
        {
            var Q0;
            Q0=makeQuery(id+"F1.opExtrude","SWEPT_FACE",FACE,{"disambiguationData":[OSD([sQuery(id+"F0.wireOp",EDGE,"E6")])]});
            var sketch = newSketch(context, id + "F39", { "sketchPlane" : qUnion([Q0])});
            skLineSegment(sketch, "E98", {"start": v(-12.48, 164.86) * mm, "end": v(32.59, 164.86) * mm, "construction": true});
            skLineSegment(sketch, "E99", {"start": v(10.05, 280) * mm, "end": v(10.05, 0) * mm, "construction": true});
            skLineSegment(sketch, "E100.bottom", {"start": v(19.05, 139.32) * mm, "end": v(1.05, 139.32) * mm});
            skLineSegment(sketch, "E100.top", {"start": v(19.05, 190.4) * mm, "end": v(1.05, 190.4) * mm});
            skLineSegment(sketch, "E100.left", {"start": v(20.05, 140.32) * mm, "end": v(20.05, 189.4) * mm});
            skLineSegment(sketch, "E100.right", {"start": v(0.05, 140.32) * mm, "end": v(0.05, 189.4) * mm});
            skPoint(sketch, "E100.middle", {"position": v(10.05, 164.86) * mm});
            skPoint(sketch, "E101.visualSharp", {"position": v(0.05, 139.32) * mm});
            skArc(sketch, "E101.filletArc", {"start": v(0.05, 140.32) * mm, "mid": v(0.35, 139.61) * mm, "end": v(1.05, 139.32) * mm});
            skPoint(sketch, "E102.visualSharp", {"position": v(20.05, 139.32) * mm});
            skArc(sketch, "E102.filletArc", {"start": v(19.05, 139.32) * mm, "mid": v(19.76, 139.61) * mm, "end": v(20.05, 140.32) * mm});
            skPoint(sketch, "E103.visualSharp", {"position": v(20.05, 190.4) * mm});
            skArc(sketch, "E103.filletArc", {"start": v(20.05, 189.4) * mm, "mid": v(19.76, 190.1) * mm, "end": v(19.05, 190.4) * mm});
            skPoint(sketch, "E104.visualSharp", {"position": v(0.05, 190.4) * mm});
            skArc(sketch, "E104.filletArc", {"start": v(1.05, 190.4) * mm, "mid": v(0.35, 190.1) * mm, "end": v(0.05, 189.4) * mm});
            skSolve(sketch);
        }
        {
            var Q0;
            Q0 = qSketchRegion(id + "F39", true);
            extrude(context, id + "F40", {"entities" : qUnion([Q0]), "operationType" : NewBodyOperationType.ADD, "depth" : 1 * mm, "offsetDistance" : 25 * mm});
        }
        {
            var Q0;
            Q0=makeQuery(id+"F38.imprint","IMPRINT",FACE,{"disambiguationData":[TD([[makeQuery(id+"F38.imprint","IMPRINT",EDGE,{"derivedFrom":sQuery(id+"F38.wireOp",EDGE,"E79.bottom")}),-1.0]])]});
            var Q1;
            Q1=makeQuery(id+"F38.imprint","IMPRINT",FACE,{"disambiguationData":[TD([[makeQuery(id+"F38.imprint","IMPRINT",EDGE,{"derivedFrom":sQuery(id+"F38.wireOp",EDGE,"E93.bottom")}),1.0]])]});
            var Q2;
            Q2=makeQuery(id+"F38.imprint","IMPRINT",FACE,{"disambiguationData":[TD([[makeQuery(id+"F38.imprint","IMPRINT",EDGE,{"derivedFrom":sQuery(id+"F38.wireOp",EDGE,"E85.bottom")}),-1.0]])]});
            extrude(context, id + "F41", {"entities" : qUnion([Q0, Q1, Q2]), "operationType" : NewBodyOperationType.ADD, "depth" : 1 * mm, "offsetDistance" : 25 * mm});
        }
        {
            var Q0;
            {var subQ0=sQuery(id+"F38.wireOp",EDGE,"E75.left");var subQ1=makeQuery(id+"F37.opExtrude","CAP_EDGE",EDGE,{"disambiguationData":[OSD([sQuery(id+"F36.wireOp",EDGE,"E71.top")])],"isStart":true});var subQ2=makeQuery(id+"F38.imprint","INTERSECT",VERTEX,{"derivedFrom":[subQ1,subQ0]});Q0=makeQuery(id+"F38.imprint","IMPRINT",FACE,{"disambiguationData":[TD([[makeQuery(id+"F38.imprint","IMPRINT",EDGE,{"disambiguationData":[TD([[subQ2,-1.0]])],"derivedFrom":subQ1}),-1.0]])]});}
            extrude(context, id + "F42", {"entities" : qUnion([Q0]), "operationType" : NewBodyOperationType.ADD, "depth" : 4 * mm, "offsetDistance" : 25 * mm});
        }
        {
            var Q0;
            {var subQ0=sQuery(id+"F38.wireOp",EDGE,"E76.top");Q0=makeQuery(id+"F38.imprint","IMPRINT",FACE,{"disambiguationData":[TD([[makeQuery(id+"F38.imprint","IMPRINT",EDGE,{"derivedFrom":subQ0}),1.0]])]});}
            extrude(context, id + "F43", {"entities" : qUnion([Q0]), "operationType" : NewBodyOperationType.ADD, "depth" : 4 * mm, "offsetDistance" : 25 * mm});
        }
        {
            var Q0;
            {var subQ5=sQuery(id+"F10.wireOp",EDGE,"E32");var subQ6=sQuery(id+"F2.wireOp",EDGE,"E12");var subQ10=sQuery(id+"F0.wireOp",EDGE,"E3");var subQ13=sQuery(id+"F3.wireOp",EDGE,"E18");Q0=makeQuery(id+"F35.boolean.opBoolean","SPLIT",FACE,{"disambiguationData":[TD([makeQuery(id+"F7.opExtrude","SWEPT_FACE",FACE,{"disambiguationData":[OSD([subQ6])]})])],"derivedFrom":makeQuery(id+"F11.boolean.opBoolean","MERGE",FACE,{"derivedFrom":[makeQuery(id+"F4.boolean.opBoolean","MERGE",FACE,{"derivedFrom":[makeQuery(id+"F1.opExtrude","SWEPT_FACE",FACE,{"disambiguationData":[OSD([subQ10])]}),makeQuery(id+"F4.opExtrude","CAP_FACE",FACE,{"disambiguationData":[OSD([sQuery(id+"F3.wireOp",EDGE,"E13"),sQuery(id+"F3.wireOp",EDGE,"E14"),sQuery(id+"F3.wireOp",EDGE,"E15"),sQuery(id+"F3.wireOp",EDGE,"E16"),sQuery(id+"F3.wireOp",EDGE,"E17"),subQ13,sQuery(id+"F3.wireOp",EDGE,"E19")])],"isStart":false})]}),makeQuery(id+"F11.opExtrude","SWEPT_FACE",FACE,{"disambiguationData":[OSD([subQ5])]})]})});}
            var sketch = newSketch(context, id + "F44", { "sketchPlane" : qUnion([Q0])});
            skLineSegment(sketch, "E105.bottom", {"start": v(80.34, 41.55) * mm, "end": v(44.34, 41.55) * mm});
            skLineSegment(sketch, "E105.top", {"start": v(80.34, 1.55) * mm, "end": v(44.34, 1.55) * mm});
            skLineSegment(sketch, "E105.left", {"start": v(82.34, 39.55) * mm, "end": v(82.34, 3.55) * mm});
            skLineSegment(sketch, "E105.right", {"start": v(42.34, 39.55) * mm, "end": v(42.34, 3.55) * mm});
            skPoint(sketch, "E105.middle", {"position": v(62.34, 21.55) * mm});
            skLineSegment(sketch, "E106.bottom", {"start": v(276.12, 41.53) * mm, "end": v(240.12, 41.53) * mm});
            skLineSegment(sketch, "E106.top", {"start": v(276.12, 1.53) * mm, "end": v(240.12, 1.53) * mm});
            skLineSegment(sketch, "E106.left", {"start": v(278.12, 39.53) * mm, "end": v(278.12, 3.53) * mm});
            skLineSegment(sketch, "E106.right", {"start": v(238.12, 39.53) * mm, "end": v(238.12, 3.53) * mm});
            skPoint(sketch, "E106.middle", {"position": v(258.12, 21.53) * mm});
            skLineSegment(sketch, "E107.bottom", {"start": v(227.98, 89.6) * mm, "end": v(231.98, 89.6) * mm});
            skLineSegment(sketch, "E107.top", {"start": v(227.98, -12.4) * mm, "end": v(231.98, -12.4) * mm});
            skLineSegment(sketch, "E107.left", {"start": v(227.98, 89.6) * mm, "end": v(227.98, -12.4) * mm});
            skLineSegment(sketch, "E107.right", {"start": v(231.98, 89.6) * mm, "end": v(231.98, -12.4) * mm});
            skPoint(sketch, "E107.middle", {"position": v(229.98, 38.6) * mm});
            skLineSegment(sketch, "E108.bottom", {"start": v(0, 70) * mm, "end": v(280, 70) * mm});
            skLineSegment(sketch, "E108.top", {"start": v(0, 74) * mm, "end": v(280, 74) * mm});
            skLineSegment(sketch, "E108.left", {"start": v(0, 70) * mm, "end": v(0, 74) * mm});
            skLineSegment(sketch, "E108.right", {"start": v(280, 70) * mm, "end": v(280, 74) * mm});
            skLineSegment(sketch, "E109.bottom", {"start": v(102, -12.27) * mm, "end": v(98, -12.27) * mm});
            skLineSegment(sketch, "E109.top", {"start": v(102, 89.73) * mm, "end": v(98, 89.73) * mm});
            skLineSegment(sketch, "E109.left", {"start": v(102, -12.27) * mm, "end": v(102, 89.73) * mm});
            skLineSegment(sketch, "E109.right", {"start": v(98, -12.27) * mm, "end": v(98, 89.73) * mm});
            skPoint(sketch, "E109.middle", {"position": v(100, 38.73) * mm});
            skPoint(sketch, "E110.visualSharp", {"position": v(238.12, 41.53) * mm});
            skArc(sketch, "E110.filletArc", {"start": v(240.12, 41.53) * mm, "mid": v(238.7, 40.94) * mm, "end": v(238.12, 39.53) * mm});
            skPoint(sketch, "E111.visualSharp", {"position": v(278.12, 41.53) * mm});
            skArc(sketch, "E111.filletArc", {"start": v(278.12, 39.53) * mm, "mid": v(277.54, 40.94) * mm, "end": v(276.12, 41.53) * mm});
            skPoint(sketch, "E112.visualSharp", {"position": v(278.12, 1.53) * mm});
            skArc(sketch, "E112.filletArc", {"start": v(276.12, 1.53) * mm, "mid": v(277.54, 2.11) * mm, "end": v(278.12, 3.53) * mm});
            skPoint(sketch, "E113.visualSharp", {"position": v(238.12, 1.53) * mm});
            skArc(sketch, "E113.filletArc", {"start": v(238.12, 3.53) * mm, "mid": v(238.7, 2.11) * mm, "end": v(240.12, 1.53) * mm});
            skPoint(sketch, "E114.visualSharp", {"position": v(42.34, 41.55) * mm});
            skArc(sketch, "E114.filletArc", {"start": v(44.34, 41.55) * mm, "mid": v(42.93, 40.97) * mm, "end": v(42.34, 39.55) * mm});
            skPoint(sketch, "E115.visualSharp", {"position": v(82.34, 41.55) * mm});
            skArc(sketch, "E115.filletArc", {"start": v(82.34, 39.55) * mm, "mid": v(81.75, 40.97) * mm, "end": v(80.34, 41.55) * mm});
            skPoint(sketch, "E116.visualSharp", {"position": v(82.34, 1.55) * mm});
            skArc(sketch, "E116.filletArc", {"start": v(80.34, 1.55) * mm, "mid": v(81.75, 2.14) * mm, "end": v(82.34, 3.55) * mm});
            skPoint(sketch, "E117.visualSharp", {"position": v(42.34, 1.55) * mm});
            skArc(sketch, "E117.filletArc", {"start": v(42.34, 3.55) * mm, "mid": v(42.93, 2.14) * mm, "end": v(44.34, 1.55) * mm});
            skSolve(sketch);
        }
        {
            var Q0;
            {var subQ5=sQuery(id+"F44.wireOp",EDGE,"E109.bottom");Q0=makeQuery(id+"F44.imprint","IMPRINT",FACE,{"disambiguationData":[TD([[makeQuery(id+"F44.imprint","IMPRINT",EDGE,{"derivedFrom":subQ5}),-1.0]])]});}
            var Q1;
            {var subQ0=sQuery(id+"F44.wireOp",EDGE,"E107.top");Q1=makeQuery(id+"F44.imprint","IMPRINT",FACE,{"disambiguationData":[TD([[makeQuery(id+"F44.imprint","IMPRINT",EDGE,{"derivedFrom":subQ0}),1.0]])]});}
            extrude(context, id + "F45", {"entities" : qUnion([Q0, Q1]), "operationType" : NewBodyOperationType.ADD, "depth" : 4 * mm, "offsetDistance" : 25 * mm});
        }
        {
            var Q0;
            Q0=makeQuery(id+"F44.imprint","IMPRINT",FACE,{"disambiguationData":[TD([[makeQuery(id+"F44.imprint","IMPRINT",EDGE,{"derivedFrom":sQuery(id+"F44.wireOp",EDGE,"E105.bottom")}),1.0]])]});
            var Q1;
            Q1=makeQuery(id+"F44.imprint","IMPRINT",FACE,{"disambiguationData":[TD([[makeQuery(id+"F44.imprint","IMPRINT",EDGE,{"derivedFrom":sQuery(id+"F44.wireOp",EDGE,"E106.bottom")}),1.0]])]});
            extrude(context, id + "F46", {"entities" : qUnion([Q0, Q1]), "operationType" : NewBodyOperationType.ADD, "depth" : 1 * mm, "offsetDistance" : 25 * mm});
        }
        {
            var Q0;
            Q0=makeQuery(id+"F37.boolean.opBoolean","MERGE",FACE,{"derivedFrom":[makeQuery(id+"F35.boolean.opBoolean","MERGE",FACE,{"derivedFrom":[makeQuery(id+"F7.boolean.opBoolean","MERGE",FACE,{"derivedFrom":[makeQuery(id+"F1.opExtrude","CAP_FACE",FACE,{"disambiguationData":[OSD([sQuery(id+"F0.wireOp",EDGE,"E1"),sQuery(id+"F0.wireOp",EDGE,"E2"),sQuery(id+"F0.wireOp",EDGE,"E3"),sQuery(id+"F0.wireOp",EDGE,"E4"),sQuery(id+"F0.wireOp",EDGE,"E5"),sQuery(id+"F0.wireOp",EDGE,"E6")])],"isStart":true}),makeQuery(id+"F7.opExtrude","CAP_FACE",FACE,{"disambiguationData":[OSD([sQuery(id+"F2.wireOp",EDGE,"E7"),sQuery(id+"F2.wireOp",EDGE,"E8"),sQuery(id+"F2.wireOp",EDGE,"E9"),sQuery(id+"F2.wireOp",EDGE,"E10"),sQuery(id+"F2.wireOp",EDGE,"E11"),sQuery(id+"F2.wireOp",EDGE,"E12")])],"isStart":true})]}),makeQuery(id+"F35.opExtrude","SWEPT_FACE",FACE,{"disambiguationData":[OSD([sQuery(id+"F34.wireOp",EDGE,"E70.right")])]})]}),makeQuery(id+"F37.opExtrude","SWEPT_FACE",FACE,{"disambiguationData":[OSD([sQuery(id+"F36.wireOp",EDGE,"E71.right")])]})]});
            var sketch = newSketch(context, id + "F47", { "sketchPlane" : qUnion([Q0])});
            skLineSegment(sketch, "E118.bottom", {"start": v(62.37, 6.25) * mm, "end": v(-7.63, 6.25) * mm});
            skLineSegment(sketch, "E118.top", {"start": v(62.37, 76.25) * mm, "end": v(-7.63, 76.25) * mm});
            skLineSegment(sketch, "E118.left", {"start": v(62.37, 6.25) * mm, "end": v(62.37, 76.25) * mm});
            skLineSegment(sketch, "E118.right", {"start": v(-7.63, 6.25) * mm, "end": v(-7.63, 76.25) * mm});
            skLineSegment(sketch, "E119", {"start": v(27.37, 76.25) * mm, "end": v(27.37, 61.16) * mm, "construction": true});
            skPoint(sketch, "E120.middle", {"position": v(27.37, 61.16) * mm});
            skLineSegment(sketch, "E121.bottom", {"start": v(46.23, 69.24) * mm, "end": v(8.52, 69.24) * mm});
            skLineSegment(sketch, "E121.top", {"start": v(46.23, 53.09) * mm, "end": v(8.52, 53.09) * mm});
            skLineSegment(sketch, "E121.left", {"start": v(46.23, 69.24) * mm, "end": v(46.23, 53.09) * mm});
            skLineSegment(sketch, "E121.right", {"start": v(8.52, 69.24) * mm, "end": v(8.52, 53.09) * mm});
            skSolve(sketch);
        }
        {
            var Q0;
            Q0=makeQuery(id+"F47.imprint","IMPRINT",FACE,{"disambiguationData":[TD([[makeQuery(id+"F47.imprint","IMPRINT",EDGE,{"derivedFrom":sQuery(id+"F47.wireOp",EDGE,"E118.bottom")}),-1.0]])]});
            extrude(context, id + "F48", {"entities" : qUnion([Q0]), "operationType" : NewBodyOperationType.ADD, "depth" : 1 * mm, "offsetDistance" : 25 * mm});
        }
        {
            var Q0;
            Q0=makeQuery(id+"F48.boolean.opBoolean","SPLIT",FACE,{"disambiguationData":[TD([makeQuery(id+"F48.opExtrude","SWEPT_FACE",FACE,{"disambiguationData":[OSD([sQuery(id+"F47.wireOp",EDGE,"E121.bottom")])]})])],"derivedFrom":makeQuery(id+"F37.boolean.opBoolean","MERGE",FACE,{"derivedFrom":[makeQuery(id+"F35.boolean.opBoolean","MERGE",FACE,{"derivedFrom":[makeQuery(id+"F7.boolean.opBoolean","MERGE",FACE,{"derivedFrom":[makeQuery(id+"F1.opExtrude","CAP_FACE",FACE,{"disambiguationData":[OSD([sQuery(id+"F0.wireOp",EDGE,"E1"),sQuery(id+"F0.wireOp",EDGE,"E2"),sQuery(id+"F0.wireOp",EDGE,"E3"),sQuery(id+"F0.wireOp",EDGE,"E4"),sQuery(id+"F0.wireOp",EDGE,"E5"),sQuery(id+"F0.wireOp",EDGE,"E6")])],"isStart":true}),makeQuery(id+"F7.opExtrude","CAP_FACE",FACE,{"disambiguationData":[OSD([sQuery(id+"F2.wireOp",EDGE,"E7"),sQuery(id+"F2.wireOp",EDGE,"E8"),sQuery(id+"F2.wireOp",EDGE,"E9"),sQuery(id+"F2.wireOp",EDGE,"E10"),sQuery(id+"F2.wireOp",EDGE,"E11"),sQuery(id+"F2.wireOp",EDGE,"E12")])],"isStart":true})]}),makeQuery(id+"F35.opExtrude","SWEPT_FACE",FACE,{"disambiguationData":[OSD([sQuery(id+"F34.wireOp",EDGE,"E70.right")])]})]}),makeQuery(id+"F37.opExtrude","SWEPT_FACE",FACE,{"disambiguationData":[OSD([sQuery(id+"F36.wireOp",EDGE,"E71.right")])]})]})});
            extrude(context, id + "F49", {"entities" : qUnion([Q0]), "operationType" : NewBodyOperationType.ADD, "depth" : 1.5 * mm, "offsetDistance" : 25 * mm});
        }
        {
            var Q0;
            Q0=makeQuery(id+"F37.boolean.opBoolean","MERGE",FACE,{"derivedFrom":[makeQuery(id+"F35.boolean.opBoolean","MERGE",FACE,{"derivedFrom":[makeQuery(id+"F11.boolean.opBoolean","MERGE",FACE,{"derivedFrom":[makeQuery(id+"F9.boolean.opBoolean","MERGE",FACE,{"derivedFrom":[makeQuery(id+"F4.boolean.opBoolean","MERGE",FACE,{"derivedFrom":[makeQuery(id+"F1.opExtrude","CAP_FACE",FACE,{"disambiguationData":[OSD([sQuery(id+"F0.wireOp",EDGE,"E1"),sQuery(id+"F0.wireOp",EDGE,"E2"),sQuery(id+"F0.wireOp",EDGE,"E3"),sQuery(id+"F0.wireOp",EDGE,"E4"),sQuery(id+"F0.wireOp",EDGE,"E5"),sQuery(id+"F0.wireOp",EDGE,"E6")])],"isStart":false}),makeQuery(id+"F4.opExtrude","SWEPT_FACE",FACE,{"disambiguationData":[OSD([sQuery(id+"F3.wireOp",EDGE,"E18")])]})]}),makeQuery(id+"F9.opExtrude","CAP_FACE",FACE,{"disambiguationData":[OSD([sQuery(id+"F8.wireOp",EDGE,"E26"),sQuery(id+"F8.wireOp",EDGE,"E27"),sQuery(id+"F8.wireOp",EDGE,"E28"),sQuery(id+"F8.wireOp",EDGE,"E29"),sQuery(id+"F8.wireOp",EDGE,"E30"),sQuery(id+"F8.wireOp",EDGE,"E31")])],"isStart":true})]}),makeQuery(id+"F11.opExtrude","CAP_FACE",FACE,{"disambiguationData":[OSD([sQuery(id+"F10.wireOp",EDGE,"E32"),sQuery(id+"F10.wireOp",EDGE,"E33"),sQuery(id+"F10.wireOp",EDGE,"E34"),sQuery(id+"F10.wireOp",EDGE,"E35"),sQuery(id+"F10.wireOp",EDGE,"E36"),sQuery(id+"F10.wireOp",EDGE,"E37")])],"isStart":true})]}),makeQuery(id+"F35.opExtrude","SWEPT_FACE",FACE,{"disambiguationData":[OSD([sQuery(id+"F34.wireOp",EDGE,"E70.left")])]})]}),makeQuery(id+"F37.opExtrude","SWEPT_FACE",FACE,{"disambiguationData":[OSD([sQuery(id+"F36.wireOp",EDGE,"E71.left")])]})]});
            var sketch = newSketch(context, id + "F50", { "sketchPlane" : qUnion([Q0])});
            skCircle(sketch, "E122", {"center": v(50.53, -7.4) * mm, "radius": 4 * mm});
            skSolve(sketch);
        }
        {
            var Q0;
            Q0 = qSketchRegion(id + "F50", true);
            extrude(context, id + "F51", {"entities" : qUnion([Q0]), "operationType" : NewBodyOperationType.ADD, "depth" : 15 * mm, "offsetDistance" : 25 * mm});
        }
        {
            var Q0;
            Q0=makeQuery(id+"F16.opPattern","COPY",FACE,{"derivedFrom":makeQuery(id+"F13.opExtrude","SWEPT_FACE",FACE,{"disambiguationData":[OSD([sQuery(id+"F12.wireOp",EDGE,"E39")])]}),"instanceName":"1"});
            var sketch = newSketch(context, id + "F52", { "sketchPlane" : qUnion([Q0])});
            skLineSegment(sketch, "E123.bottom", {"start": v(-81.88, -69.84) * mm, "end": v(-61.88, -69.84) * mm});
            skLineSegment(sketch, "E123.top", {"start": v(-81.88, -49.84) * mm, "end": v(-61.88, -49.84) * mm});
            skLineSegment(sketch, "E123.left", {"start": v(-81.88, -69.84) * mm, "end": v(-81.88, -49.84) * mm});
            skLineSegment(sketch, "E123.right", {"start": v(-61.88, -69.84) * mm, "end": v(-61.88, -49.84) * mm});
            skPoint(sketch, "E123.middle", {"position": v(-71.88, -59.84) * mm});
            skPoint(sketch, "E123.middle.positionSnap0", {"position": v(-71.88, -63.1) * mm});
            skPoint(sketch, "E123.centerSnap0", {"position": v(-71.88, -63.1) * mm});
            skLineSegment(sketch, "E124.bottom", {"start": v(82.3, -70.07) * mm, "end": v(62.3, -70.07) * mm});
            skLineSegment(sketch, "E124.top", {"start": v(82.3, -50.07) * mm, "end": v(62.3, -50.07) * mm});
            skLineSegment(sketch, "E124.left", {"start": v(82.3, -70.07) * mm, "end": v(82.3, -50.07) * mm});
            skLineSegment(sketch, "E124.right", {"start": v(62.3, -70.07) * mm, "end": v(62.3, -50.07) * mm});
            skPoint(sketch, "E124.middle", {"position": v(72.3, -60.07) * mm});
            skLineSegment(sketch, "E125.bottom", {"start": v(81.6, -243.9) * mm, "end": v(61.6, -243.9) * mm});
            skLineSegment(sketch, "E125.top", {"start": v(81.6, -223.9) * mm, "end": v(61.6, -223.9) * mm});
            skLineSegment(sketch, "E125.left", {"start": v(81.6, -243.9) * mm, "end": v(81.6, -223.9) * mm});
            skLineSegment(sketch, "E125.right", {"start": v(61.6, -243.9) * mm, "end": v(61.6, -223.9) * mm});
            skPoint(sketch, "E125.middle", {"position": v(71.6, -233.9) * mm});
            skLineSegment(sketch, "E126.bottom", {"start": v(-61.84, -223.5) * mm, "end": v(-81.84, -223.5) * mm});
            skLineSegment(sketch, "E126.top", {"start": v(-61.84, -243.5) * mm, "end": v(-81.84, -243.5) * mm});
            skLineSegment(sketch, "E126.left", {"start": v(-61.84, -223.5) * mm, "end": v(-61.84, -243.5) * mm});
            skLineSegment(sketch, "E126.right", {"start": v(-81.84, -223.5) * mm, "end": v(-81.84, -243.5) * mm});
            skPoint(sketch, "E126.middle", {"position": v(-71.84, -233.5) * mm});
            skSolve(sketch);
        }
        {
            var Q0;
            Q0 = qSketchRegion(id + "F52", true);
            extrude(context, id + "F53", {"entities" : qUnion([Q0]), "depth" : 2 * mm, "offsetDistance" : 25 * mm});
        }
        {
            var Q0;
            Q0=makeQuery(id+"F4.opExtrude","SWEPT_FACE",FACE,{"disambiguationData":[OSD([sQuery(id+"F3.wireOp",EDGE,"E17")])]});
            var sketch = newSketch(context, id + "F54", { "sketchPlane" : qUnion([Q0])});
            skLineSegment(sketch, "E127", {"start": v(59.67, -20) * mm, "end": v(73, -2.6) * mm});
            skPoint(sketch, "E127.endSnap0", {"position": v(71, -2.6) * mm});
            skLineSegment(sketch, "E128", {"start": v(73, -2.6) * mm, "end": v(73, 1.84) * mm});
            skLineSegment(sketch, "E129", {"start": v(73, 1.84) * mm, "end": v(-72.48, 1.84) * mm});
            skLineSegment(sketch, "E130", {"start": v(-59.67, -20) * mm, "end": v(59.67, -20) * mm});
            skLineSegment(sketch, "E131", {"start": v(-72.48, 1.84) * mm, "end": v(-72.48, 0.84) * mm});
            skLineSegment(sketch, "E132", {"start": v(-72.48, 0.84) * mm, "end": v(-65.42, -12.5) * mm});
            skLineSegment(sketch, "E133", {"start": v(-65.42, -12.5) * mm, "end": v(-59.67, -20) * mm});
            skSolve(sketch);
        }
        {
            var Q0;
            Q0 = qSketchRegion(id + "F54", true);
            extrude(context, id + "F55", {"entities" : qUnion([Q0]), "operationType" : NewBodyOperationType.ADD, "depth" : 2.62 * mm, "offsetDistance" : 25 * mm});
        }
        {
            var Q0;
            Q0=makeQuery(id+"F33.opExtrude","SWEPT_FACE",FACE,{"disambiguationData":[OSD([sQuery(id+"F32.wireOp",EDGE,"E66.top")])]});
            var sketch = newSketch(context, id + "F56", { "sketchPlane" : qUnion([Q0])});
            skLineSegment(sketch, "E134.bottom", {"start": v(-49.53, -286.57) * mm, "end": v(-51.53, -286.57) * mm});
            skLineSegment(sketch, "E134.top", {"start": v(-49.53, -294.57) * mm, "end": v(-51.53, -294.57) * mm});
            skLineSegment(sketch, "E134.left", {"start": v(-49.53, -286.57) * mm, "end": v(-49.53, -294.57) * mm});
            skLineSegment(sketch, "E134.right", {"start": v(-51.53, -286.57) * mm, "end": v(-51.53, -294.57) * mm});
            skPoint(sketch, "E134.middle", {"position": v(-50.53, -290.57) * mm});
            skSolve(sketch);
        }
        {
            var Q0;
            Q0 = qSketchRegion(id + "F56", true);
            extrude(context, id + "F57", {"entities" : qUnion([Q0]), "operationType" : NewBodyOperationType.REMOVE, "oppositeDirection" : true, "depth" : 11 * mm, "offsetDistance" : 25 * mm});
        }
        {
            var Q0;
            Q0=makeQuery(id+"F57.boolean.opBoolean","COPY",EDGE,{"derivedFrom":makeQuery(id+"F57.opExtrude","SWEPT_EDGE",EDGE,{"disambiguationData":[OSD([sQuery(id+"F56.wireOp",EDGE,"E134.bottom"),sQuery(id+"F56.wireOp",EDGE,"E134.left")])]})});
            var Q1;
            Q1=makeQuery(id+"F57.boolean.opBoolean","COPY",EDGE,{"derivedFrom":makeQuery(id+"F57.opExtrude","SWEPT_EDGE",EDGE,{"disambiguationData":[OSD([sQuery(id+"F56.wireOp",EDGE,"E134.bottom"),sQuery(id+"F56.wireOp",EDGE,"E134.right")])]})});
            var Q2;
            Q2=makeQuery(id+"F57.boolean.opBoolean","COPY",EDGE,{"derivedFrom":makeQuery(id+"F57.opExtrude","SWEPT_EDGE",EDGE,{"disambiguationData":[OSD([sQuery(id+"F56.wireOp",EDGE,"E134.top"),sQuery(id+"F56.wireOp",EDGE,"E134.right")])]})});
            var Q3;
            Q3=makeQuery(id+"F57.boolean.opBoolean","COPY",EDGE,{"derivedFrom":makeQuery(id+"F57.opExtrude","SWEPT_EDGE",EDGE,{"disambiguationData":[OSD([sQuery(id+"F56.wireOp",EDGE,"E134.top"),sQuery(id+"F56.wireOp",EDGE,"E134.left")])]})});
            fillet(context, id + "F58", {"entities" : qUnion([Q0, Q1, Q2, Q3]), "radius" : 0.9 * mm, "tangentPropagation" : true, "allowEdgeOverflow" : false});
        }
    });
